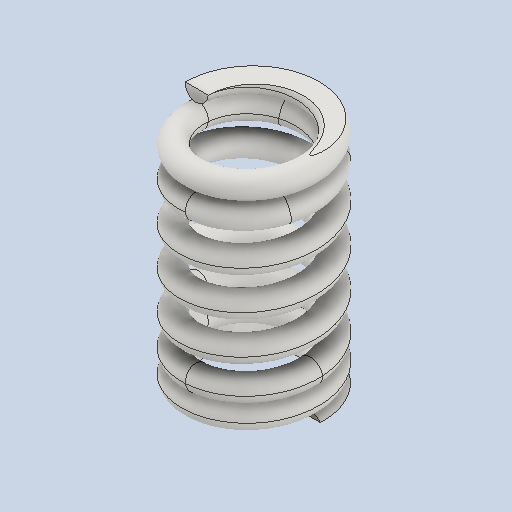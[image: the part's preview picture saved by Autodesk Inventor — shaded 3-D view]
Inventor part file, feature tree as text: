
AUTODESK INVENTOR PART (.ipt)
format: ipt  version: 2022 (Build 260153000, 153)  size: 1,047,552 bytes
history: native  units: mm
features: other x41, sketch x31, extrude x8, helix x4, sweep x2
ambient origin geometry x8: Origin, YZ Plane, XZ Plane, XY Plane, X Axis, Y Axis, Z Axis, Center Point
bodies: Solid1 (feature_tree)
feature tree (86):
  other  "Caminho helicoidal principal (direita)"
  other  "Plano de trabalho de seção (direita)"
  other  "Plano de trabalho inicial (direita)"
  other  "Plano de trabalho final (direita)"
  other  "Plano de trabalho de corte final (direita)"
  other  "Plano de trabalho de corte inicial (direita)"
  other  "Plano de trabalho de corte final normal 1 (direita)"
  other  "Plano de trabalho de corte final normal 2 (direita)"
  sweep  "Main Coil Feature(R)"
  other  "Espiral de transição inicial 1 (direita)"
  helix  "Coil  Start Transition 2(R)"  [1 undecoded]
  helix  "Coil  Start Transition 3(R)"  [1 undecoded]
  helix  "Coil  Start Transition 4(R)"  [1 undecoded]
  other  "Espiral de extremidades iniciais (direita)"
  extrude  "Operação de corte inicial (direita)"  Depth=10.0mm
  other  "Espiral de transição final 1 (direita)"
  other  "Espiral de transição final 2 (direita)"
  other  "Espiral de transição final 3 (direita)"
  other  "Espiral de transição final 4 (direita)"
  other  "Espiral final (direita)"
  extrude  "Operação de corte final (direita)"  Depth=10.0mm
  extrude  "Operação de corte de extremidades normais 1 (direita)"  Depth=6.0mm
  extrude  "Plain Ends Cut  2(R)"  Depth=6.0mm
  other  "Caminho helicoidal principal (esquerda)"
  other  "Plano de trabalho de seção (esquerda)"
  other  "Plano de trabalho inicial (esquerda)"
  other  "Plano de trabalho final (esquerda)"
  other  "Plano de trabalho de corte final (esquerda)"
  other  "Plano de trabalho de corte inicial (esquerda)"
  other  "Plano de trabalho de corte de extremidades normais 1 (esquerda)"
  other  "Plano de trabalho de corte de extremidades normais 2 (esquerda)"
  sweep  "Main Coil Feature(L)"
  other  "Espiral de transição inicial 1 (esquerda)"
  other  "Espiral de transição inicial 2 (esquerda)"
  other  "Espiral de transição inicial 3 (esquerda)"
  other  "Espiral de transição inicial 4 (esquerda)"
  other  "Espiral de extremidades iniciais (esquerda)"
  extrude  "Operação de corte inicial (esquerda)"  TaperAngle=0.0deg  [1 undecoded]
  helix  "Coil End Transition 1(L)"  [1 undecoded]
  other  "Espiral de transição final 2 (esquerda)"
  other  "Espiral de transição final 3 (esquerda)"
  other  "Espiral de transição final 4 (esquerda)"
  other  "Espiral final (esquerda)"
  extrude  "Operação de corte final (esquerda)"  Depth=0.25mm
  extrude  "Cut Plain Ends Cut 1(L)"  Depth=10.0mm
  extrude  "Cut Plain Ends Cut 2(L)"  Depth=1.942655mm
  other  "Plano de trabalho baseado em iMate"
  other  "Visualização do centro"
  other  "Vissualiação do eixo X"
  sketch  "Esboço de corte de caminho (direita)"  dims[d0=0.25mm d2=1.684938mm d3=10.0mm d4=32.5mm]
  other  "Srf1"
  sketch  "Esboço de corte helicoidal (direita)"  dims[d5=0.0mm d6=90.0deg d7=90.0deg d8=0.0mm d9=0.0mm d12=1.942655mm d13=-2.508302mm d14=1.0mm]
  sketch  "Esboço helicoidal de transição inicial 1 (direita)"  dims[d15=0.0mm]
  sketch  "Sketch  Start Transition 2(R)"  dims[d16=1.513704mm d17=10.0mm d18=2.5mm d19=0.0mm d20=90.0deg d21=90.0deg d22=0.0mm d23=0.0mm]
  sketch  "Sketch  Start Transition 3(R)"  dims[d24=1.342469mm d25=10.0mm d26=2.5mm d27=0.0mm d28=90.0deg d29=90.0deg d30=0.0mm d31=0.0mm]
  sketch  "Sketch  Start Transition 4(R)"  dims[d32=1.171235mm d33=10.0mm d34=2.5mm d35=0.0mm d36=90.0deg d37=90.0deg d38=0.0mm d39=0.0mm]
  sketch  "Esboço helicoidal de transição final 1 (direita)"  dims[d40=1.0mm d41=10.0mm d42=2.5mm d43=0.0mm d44=90.0deg d45=90.0deg d46=0.0mm d47=0.0mm]
  sketch  "Esboço helicoidal de transição final 2 (direita)"  dims[d48=1.513704mm d49=10.0mm d50=1.875mm d51=0.0mm d52=90.0deg d53=90.0deg d54=0.0mm d55=0.0mm]
  sketch  "Esboço helicoidal de transição final 3 (direita)"  dims[d56=1.342469mm d57=10.0mm d58=1.875mm d59=0.0mm d60=90.0deg d61=90.0deg d62=0.0mm d63=0.0mm]
  sketch  "Esboço helicoidal de transição final 4 (direita)"  dims[d64=1.171235mm d65=10.0mm d66=1.875mm d67=0.0mm d68=90.0deg d69=90.0deg d70=0.0mm d71=0.0mm]
  sketch  "Esboço de extremidades iniciais (direita)"  dims[d72=1.0mm d73=10.0mm d74=1.875mm d75=0.0mm d76=90.0deg d77=90.0deg d78=0.0mm d79=0.0mm d81=10.0mm d82=15.0mm]
  sketch  "Esboço helicoidal final (direita)"  dims[d83=0.0mm d84=90.0deg d85=90.0deg d86=0.0mm d87=0.0mm d88=1.005737mm d89=10.0mm d90=10.0mm]
  sketch  "Esboço de corte final (direita)"  dims[d91=0.0mm d92=90.0deg d93=90.0deg d94=0.0mm d95=0.0mm d96=6.0mm]
  sketch  "Esboço de corte inicial (direita)"  dims[d97=1.005737mm d98=0.0mm d99=6.0mm]
  sketch  "Esboço de corte de caminho (esquerda)"  dims[d100=1.005737mm d101=0.0mm]
  other  "Srf2"
  sketch  "Esboço de corte helicoidal (esquerda)"  dims[d102=0.0mm d103=0.0mm d104=0.0mm d105=0.0mm d106=0.0mm d108=0.0mm d112=0.0mm d113=0.0mm d114=0.0mm d121=0.257154mm]
  sketch  "Esboço helicoidal de transição inicial 1 (esquerda)"  dims[d131=0.0mm d132=0.0mm d133=0.0mm]
  sketch  "Esboço helicoidal de transição inicial 2 (esquerda)"  dims[d134=0.0mm d135=0.25mm]
  sketch  "Esboço helicoidal de transição inicial 3 (esquerda)"  dims[d137=1.684938mm d138=10.0mm d139=32.5mm]
  sketch  "Esboço helicoidal de transição inicial 4 (esquerda)"  dims[d140=0.0mm d141=90.0deg d142=90.0deg d143=0.0mm d144=0.0mm d145=1.942655mm]
  sketch  "Esboço de extremidades iniciais (esquerda)"  dims[d146=-2.508302mm]
  sketch  "Esboço de corte inicial (esquerda)"  dims[d147=0.257154mm]
  sketch  "Esboço helicoidal de transição final 1 (esquerda)"  dims[d148=0.00572mm]
  sketch  "Esboço helicoidal de transição final 2 (esquerda)"  dims[d149=1.0mm]
  other  "Esoço helicoidal de transição final 3 (esquerda)"
  sketch  "Esboço helicoidal de transição final 4 (esquerda)"  dims[d150=0.0mm]
  sketch  "Esboço helicoidal final (esquerda)"  dims[d151=0.0mm]
  sketch  "Esboço de corte final (esquerda)"  dims[d152=1.513704mm d153=10.0mm d154=2.5mm d155=0.0mm d156=90.0deg d157=90.0deg d158=0.0mm d159=0.0mm]
  sketch  "Esboço de corte de extremidades normais 2 (esquerda)"  dims[d160=1.342469mm]
  sketch  "Esboço de corte de extremidades normais 2 (direita)"  dims[d161=10.0mm d162=2.5mm d163=0.0mm d164=90.0deg d165=90.0deg d166=0.0mm d167=0.0mm]
  sketch  "Esboço de corte de extremidades normais 1 (direita)"  dims[d168=1.171235mm]
  sketch  "Esboço de corte de extremidades normais 1 (esquerda)"  dims[d169=10.0mm d170=2.5mm d171=0.0mm d172=90.0deg d173=90.0deg d174=0.0mm d175=0.0mm d176=1.0mm d177=10.0mm d178=2.5mm d179=0.0mm d180=90.0deg d181=90.0deg d182=0.0mm d183=0.0mm d184=10.0mm d185=10.0mm d186=10.0mm d187=10.0mm d188=1.005737mm d189=10.0mm d190=15.0mm d191=0.0mm d192=90.0deg d193=90.0deg d194=0.0mm d195=0.0mm d196=10.0mm d197=6.0mm d198=1.005737mm d199=0.0mm d200=10.0mm d201=1.513704mm d202=10.0mm d203=1.875mm d204=0.0mm d205=90.0deg d206=90.0deg d207=0.0mm d208=0.0mm d209=10.0mm d210=1.342469mm d211=10.0mm d212=1.875mm d213=0.0mm d214=90.0deg d215=90.0deg d216=0.0mm d217=0.0mm d218=1.171235mm d219=10.0mm d220=1.875mm d221=0.0mm d222=90.0deg d223=90.0deg d224=0.0mm d225=0.0mm d226=1.0mm d227=10.0mm d228=1.875mm d229=0.0mm d230=90.0deg d231=90.0deg d232=0.0mm d233=0.0mm d234=10.0mm d235=10.0mm d236=10.0mm d237=1.005737mm d238=10.0mm d239=10.0mm d240=0.0mm d241=90.0deg d242=90.0deg d243=0.0mm d244=0.0mm d245=6.0mm d246=1.005737mm d247=0.0mm d248=10.0mm d249=10.0mm d254=6.0mm d255=10.0mm d256=0.0mm d257=20.0mm d258=-0.00572mm d259=6.0mm d260=10.0mm d261=0.0mm d262=10.0mm d263=6.0mm d264=10.0mm d265=0.0mm d266=10.0mm d267=0.0mm d270=-2.383302mm d271=0.0mm d272=6.0mm d273=10.0mm d274=0.0mm d275=20.0mm d276=-157.079633mm d277=5.0mm d278=5.0mm d279=0.0mm d280=0.0mm]
  other  "Seção inicial do Plano de trabalho"
  other  "Curva básica (direita)"
  other  "Curva básica (esquerda)"
note: 5 required parameter values undecoded (feature->parameter linkage not recoverable at this tier; creation-order binding heuristic only, values carry confidence <= 0.55)
